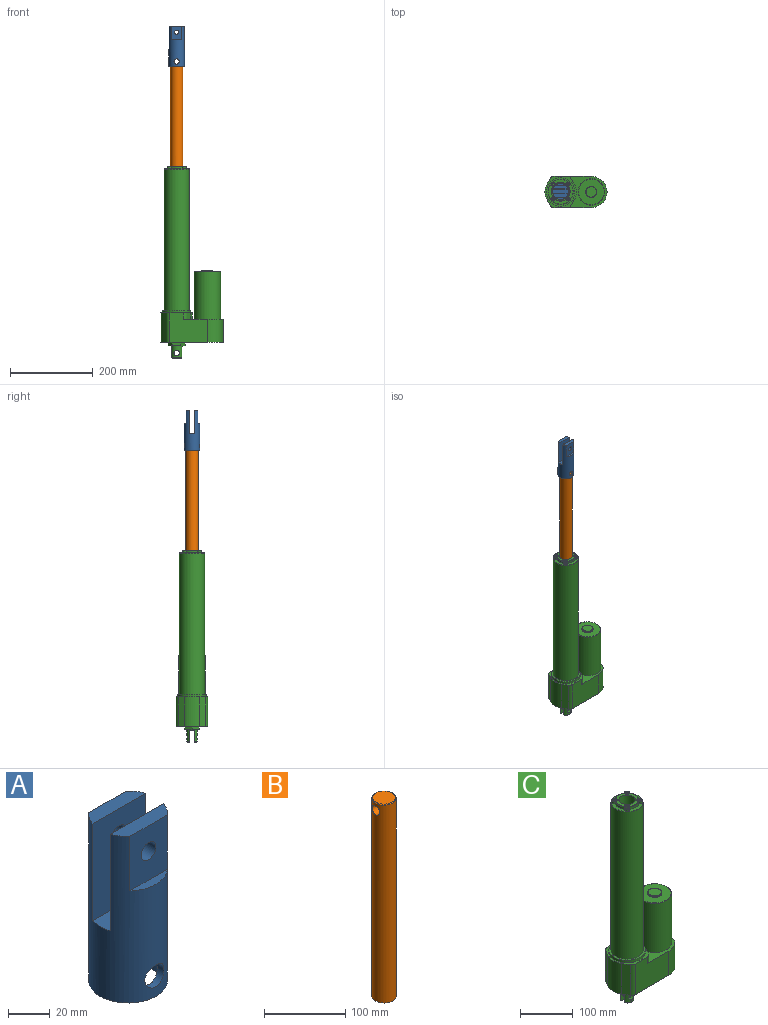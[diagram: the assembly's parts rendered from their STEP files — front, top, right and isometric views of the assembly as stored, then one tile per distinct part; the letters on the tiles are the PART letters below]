
ASSEMBLY  parts=3 mates=2
PART A: 17 faces, bbox 38x38x98 mm
  f0: plane 36.06x8mm, normal (0,0,1), area 254.7mm2, adj f2,f5,f9
  f1: plane 36.06x8mm, normal (0,0,1), area 254.7mm2, adj f2,f4,f7
  f2: cylinder r=19mm len=98mm, axis (0,0,-1), area 8232.8mm2, adj f0,f1,f3,f4,f5,f6,f7,f8
  f3: plane 38x38mm, normal (0,0,-1), area 427.3mm2, adj f2,f11
  f4: plane 57x36.06mm, normal (0,1,0), area 1976.6mm2, adj f1,f2,f6,f14
  f5: plane 57x36.06mm, normal (0,-1,0), area 1976.6mm2, adj f0,f2,f6,f13
  f6: plane 38x12mm, normal (0,0,1), area 448.3mm2, adj f2,f4,f5
  f7: plane 32x25.69mm, normal (0,-1,0), area 743.6mm2, adj f1,f2,f8,f14
  f8: plane 25.69x5mm, normal (0,0,1), area 88.2mm2, adj f2,f7
  f9: plane 32x25.69mm, normal (0,1,0), area 743.6mm2, adj f0,f2,f10,f13
  f10: plane 25.69x5mm, normal (0,0,1), area 88.2mm2, adj f2,f9
  f11: cylinder r=15mm len=31mm, axis (0,0,-1), area 2649.2mm2, adj f3,f12,f15,f16
  f12: plane 30x30mm, normal (0,0,-1), area 706.9mm2, adj f11
  f13: cylinder r=5mm len=10mm, axis (0,-1,0), area 251.3mm2, adj f5,f9
  f14: cylinder r=5mm len=10mm, axis (0,-1,0), area 251.3mm2, adj f4,f7
  f15: cylinder r=6.5mm len=13mm, axis (0,-1,0), area 169.9mm2, adj f2,f11
  f16: cylinder r=6.5mm len=13mm, axis (0,-1,0), area 170.1mm2, adj f2,f11
PART B: 5 faces, bbox 30x30x300 mm
  f0: cylinder r=15mm len=299mm, axis (0,0,-1), area 27907.9mm2, adj f2,f3,f4
  f1: plane 28x28mm, normal (0,0,1), area 615.8mm2, adj f4
  f2: plane 30x30mm, normal (0,0,-1), area 706.9mm2, adj f0
  f3: cylinder r=6.5mm len=30mm, axis (1,0,0), area 1165.5mm2, adj f0
  f4: cone r=14mm half-angle=45deg, axis (0,0,-1), area 128.8mm2, adj f0,f1
PART C: 105 faces, bbox 150x76x463 mm
  f0: cylinder r=13mm len=29mm, axis (0,0,1), area 1519.5mm2, adj f2,f97,f99,f100,f101,f102,f103,f104
  f1: plane 21.82x7mm, normal (0,0,-1), area 109.8mm2, adj f2,f100
  f2: cone r=12mm half-angle=45deg, axis (0,0,1), area 41mm2, adj f0,f1,f100
  f3: plane 60x60mm, normal (0,0,1), area 1007.8mm2, adj f29,f30,f31,f32,f33,f34,f35,f36
  f4: plane 150x76mm, normal (0,0,-1), area 8495.4mm2, adj f6,f7,f8,f20,f21,f22,f23,f24
  f5: plane 95.83x76mm, normal (0,0,1), area 2262.5mm2, adj f6,f7,f8,f9,f15,f16,f17,f18
  f6: plane 90.17x71mm, normal (0,-1,0), area 5534.3mm2, adj f4,f5,f7,f15,f24,f25
  f7: cylinder r=38mm len=76mm, axis (0,0,-1), area 6685.3mm2, adj f4,f5,f6,f8
  f8: plane 90.17x71mm, normal (0,1,0), area 5534.3mm2, adj f4,f5,f7,f19,f20,f25
  f9: cylinder r=32mm len=114mm, axis (0,0,-1), area 22921.1mm2, adj f5,f14
  f10: plane 62x62mm, normal (0,0,1), area 2446.5mm2, adj f11,f14
  f11: cylinder r=13.5mm len=27mm, axis (0,0,-1), area 169.6mm2, adj f10,f13
  f12: plane 25x25mm, normal (0,0,1), area 490.9mm2, adj f13
  f13: torus R=12.5mm, axis (0,0,1), area 129.7mm2, adj f11,f12
  f14: torus R=31mm, axis (0,0,1), area 312.2mm2, adj f9,f10
  f15: cylinder r=10mm len=15mm, axis (0,0,-1), area 157.1mm2, adj f5,f6,f16,f25
  f16: plane 15x14mm, normal (0.87,-0.5,0), area 242.5mm2, adj f5,f15,f17,f25
  f17: cylinder r=38mm len=38mm, axis (0,0,-1), area 596.9mm2, adj f5,f16,f18,f25
  f18: plane 15x14mm, normal (0.87,0.5,0), area 242.5mm2, adj f5,f17,f19,f25
  f19: cylinder r=10mm len=15mm, axis (0,0,-1), area 157.1mm2, adj f5,f8,f18,f25
  f20: cylinder r=10mm len=71mm, axis (0,0,-1), area 743.5mm2, adj f4,f8,f21,f25
  f21: plane 71x14mm, normal (-0.87,0.5,0), area 1147.8mm2, adj f4,f20,f22,f25
  f22: cylinder r=38mm len=71mm, axis (0,0,-1), area 2825.3mm2, adj f4,f21,f23,f25
  f23: plane 71x14mm, normal (-0.87,-0.5,0), area 1147.8mm2, adj f4,f22,f24,f25
  f24: cylinder r=10mm len=71mm, axis (0,0,-1), area 743.5mm2, adj f4,f6,f23,f25
  f25: plane 76x76mm, normal (0,0,1), area 1086.1mm2, adj f6,f8,f15,f16,f17,f18,f19,f20
  f26: cylinder r=30.5mm len=341.5mm, axis (0,0,-1), area 65444.1mm2, adj f27,f86
  f27: plane 69x69mm, normal (0,0,1), area 816.8mm2, adj f26,f28
  f28: cylinder r=34.5mm len=69mm, axis (0,0,-1), area 1300.6mm2, adj f25,f27
  f29: cylinder r=5.5mm len=7.17mm, axis (0,0,-1), area 60.2mm2, adj f3,f30,f36,f83
  f30: cylinder r=23mm len=24.87mm, axis (0,0,-1), area 131.4mm2, adj f3,f29,f31,f85
  f31: cylinder r=5.5mm len=7.17mm, axis (0,0,-1), area 60.2mm2, adj f3,f30,f32,f84
  f32: cylinder r=23mm len=24.87mm, axis (0,0,-1), area 131.4mm2, adj f3,f31,f33,f82
  f33: cylinder r=5.5mm len=7.17mm, axis (0,0,-1), area 60.2mm2, adj f3,f32,f34,f80
  f34: cylinder r=23mm len=24.87mm, axis (0,0,-1), area 131.4mm2, adj f3,f33,f35,f78
  f35: cylinder r=5.5mm len=7.17mm, axis (0,0,-1), area 60.2mm2, adj f3,f34,f36,f79
  f36: cylinder r=23mm len=24.87mm, axis (0,0,-1), area 131.4mm2, adj f3,f29,f35,f81
  f37: plane 44x44mm, normal (0,0,1), area 661.1mm2, adj f78,f79,f80,f81,f82,f83,f84,f85
  f38: cylinder r=4.5mm len=9mm, axis (0,0,-1), area 141.4mm2, adj f3,f76
  f39: plane 7x7mm, normal (0,0,1), area 24.6mm2, adj f67,f68,f69,f70,f71,f72,f76
  f40: cylinder r=4.5mm len=9mm, axis (0,0,-1), area 141.4mm2, adj f3,f77
  f41: plane 7x7mm, normal (0,0,1), area 24.6mm2, adj f60,f61,f62,f63,f64,f65,f77
  f42: cylinder r=4.5mm len=9mm, axis (0,0,-1), area 141.4mm2, adj f3,f74
  f43: plane 7x7mm, normal (0,0,1), area 24.6mm2, adj f53,f54,f55,f56,f57,f58,f74
  f44: cylinder r=4.5mm len=9mm, axis (0,0,-1), area 141.4mm2, adj f3,f75
  f45: plane 7x7mm, normal (0,0,1), area 24.6mm2, adj f46,f47,f48,f49,f50,f51,f75
  f46: plane 3x2.08mm, normal (0.44,0.9,0), area 6.9mm2, adj f45,f47,f51,f52
  f47: plane 3x1.92mm, normal (-0.56,0.83,0), area 6.9mm2, adj f45,f46,f48,f52
  f48: plane 3x2.3mm, normal (-1,-0.07,0), area 6.9mm2, adj f45,f47,f49,f52
  f49: plane 3x2.08mm, normal (-0.44,-0.9,0), area 6.9mm2, adj f45,f48,f50,f52
  f50: plane 3x1.92mm, normal (0.56,-0.83,0), area 6.9mm2, adj f45,f49,f51,f52
  f51: plane 3x2.3mm, normal (1,0.07,0), area 6.9mm2, adj f45,f46,f50,f52
  f52: plane 4.61x4.15mm, normal (0,0,1), area 13.9mm2, adj f46,f47,f48,f49,f50,f51
  f53: plane 3x2.08mm, normal (0.44,0.9,0), area 6.9mm2, adj f43,f54,f58,f59
  f54: plane 3x1.92mm, normal (-0.56,0.83,0), area 6.9mm2, adj f43,f53,f55,f59
  f55: plane 3x2.3mm, normal (-1,-0.07,0), area 6.9mm2, adj f43,f54,f56,f59
  f56: plane 3x2.08mm, normal (-0.44,-0.9,0), area 6.9mm2, adj f43,f55,f57,f59
  f57: plane 3x1.92mm, normal (0.56,-0.83,0), area 6.9mm2, adj f43,f56,f58,f59
  f58: plane 3x2.3mm, normal (1,0.07,0), area 6.9mm2, adj f43,f53,f57,f59
  f59: plane 4.61x4.15mm, normal (0,0,1), area 13.9mm2, adj f53,f54,f55,f56,f57,f58
  f60: plane 3x2.07mm, normal (0.45,0.89,0), area 6.9mm2, adj f41,f61,f65,f66
  f61: plane 3x1.93mm, normal (-0.55,0.83,0), area 6.9mm2, adj f41,f60,f62,f66
  f62: plane 3x2.31mm, normal (-1,-0.06,0), area 6.9mm2, adj f41,f61,f63,f66
  f63: plane 3x2.07mm, normal (-0.45,-0.89,0), area 6.9mm2, adj f41,f62,f64,f66
  f64: plane 3x1.93mm, normal (0.55,-0.83,0), area 6.9mm2, adj f41,f63,f65,f66
  f65: plane 3x2.31mm, normal (1,0.06,0), area 6.9mm2, adj f41,f60,f64,f66
  f66: plane 4.61x4.13mm, normal (0,0,1), area 13.9mm2, adj f60,f61,f62,f63,f64,f65
  f67: plane 3x2.31mm, normal (0,1,0), area 6.9mm2, adj f39,f68,f72,f73
  f68: plane 3x2mm, normal (-0.87,0.5,0), area 6.9mm2, adj f39,f67,f69,f73
  f69: plane 3x2mm, normal (-0.87,-0.5,0), area 6.9mm2, adj f39,f68,f70,f73
  f70: plane 3x2.31mm, normal (0,-1,0), area 6.9mm2, adj f39,f69,f71,f73
  f71: plane 3x2mm, normal (0.87,-0.5,0), area 6.9mm2, adj f39,f70,f72,f73
  f72: plane 3x2mm, normal (0.87,0.5,0), area 6.9mm2, adj f39,f67,f71,f73
  f73: plane 4.62x4mm, normal (0,0,1), area 13.9mm2, adj f67,f68,f69,f70,f71,f72
  f74: torus R=3.5mm, axis (0,0,1), area 40.8mm2, adj f42,f43
  f75: torus R=3.5mm, axis (0,0,1), area 40.8mm2, adj f44,f45
  f76: torus R=3.5mm, axis (0,0,1), area 40.8mm2, adj f38,f39
  f77: torus R=3.5mm, axis (0,0,1), area 40.8mm2, adj f40,f41
  f78: torus R=22mm, axis (0,0,1), area 39.5mm2, adj f34,f37,f79,f80
  f79: torus R=6.5mm, axis (0,0,1), area 19mm2, adj f35,f37,f78,f81
  f80: torus R=6.5mm, axis (0,0,1), area 19mm2, adj f33,f37,f78,f82
  f81: torus R=22mm, axis (0,0,1), area 39.5mm2, adj f36,f37,f79,f83
  f82: torus R=22mm, axis (0,0,1), area 39.5mm2, adj f32,f37,f80,f84
  f83: torus R=6.5mm, axis (0,0,1), area 19mm2, adj f29,f37,f81,f85
  f84: torus R=6.5mm, axis (0,0,1), area 19mm2, adj f31,f37,f82,f85
  f85: torus R=22mm, axis (0,0,1), area 39.5mm2, adj f30,f37,f83,f84
  f86: torus R=30mm, axis (0,0,1), area 149.6mm2, adj f3,f26
  f87: cylinder r=15.5mm len=330mm, axis (0,0,1), area 32138.5mm2, adj f37,f88
  f88: plane 31x31mm, normal (0,0,1), area 754.8mm2, adj f87
  f89: cylinder r=24mm len=48mm, axis (0,0,1), area 150.8mm2, adj f4,f90
  f90: plane 48x48mm, normal (0,0,-1), area 748.7mm2, adj f89,f91,f92,f93,f94,f95,f96
  f91: plane 20.21x7mm, normal (0,1,0), area 141.5mm2, adj f90,f92,f96,f97
  f92: plane 17.5x10.1mm, normal (0.87,0.5,0), area 141.5mm2, adj f90,f91,f93,f97
  f93: plane 17.5x10.1mm, normal (0.87,-0.5,0), area 141.5mm2, adj f90,f92,f94,f97
  f94: plane 20.21x7mm, normal (0,-1,0), area 141.5mm2, adj f90,f93,f95,f97
  f95: plane 17.5x10.1mm, normal (-0.87,-0.5,0), area 141.5mm2, adj f90,f94,f96,f97
  f96: plane 17.5x10.1mm, normal (-0.87,0.5,0), area 141.5mm2, adj f90,f91,f95,f97
  f97: plane 40.41x35mm, normal (0,0,-1), area 530mm2, adj f0,f91,f92,f93,f94,f95,f96
  f98: plane 21.82x7mm, normal (0,0,-1), area 109.8mm2, adj f99,f101
  f99: cone r=12mm half-angle=45deg, axis (0,0,1), area 41mm2, adj f0,f98,f101
  f100: plane 29.02x24.02mm, normal (0,-1,0), area 562.2mm2, adj f0,f1,f2,f102,f104
  f101: plane 29.02x24.02mm, normal (0,1,0), area 562.2mm2, adj f0,f98,f99,f102,f103
  f102: plane 26x10mm, normal (0,0,-1), area 253.4mm2, adj f0,f100,f101
  f103: cylinder r=6.5mm len=13mm, axis (0,1,0), area 291.8mm2, adj f0,f101
  f104: cylinder r=6.5mm len=13mm, axis (0,1,0), area 291.8mm2, adj f0,f100
PLACE A t=(-37,0,687.5)mm
PLACE B rot(axis=(0,0,1),90deg) t=(-37,0,362.5)mm
PLACE C at identity fixed
MATE fastened A.f11 <-> B.f0  axis (0,0,-1) through (-37,0,638.5)mm
MATE slider B.f0 <-> C.f87  axis (0,0,-1) through (-37,0,512)mm
